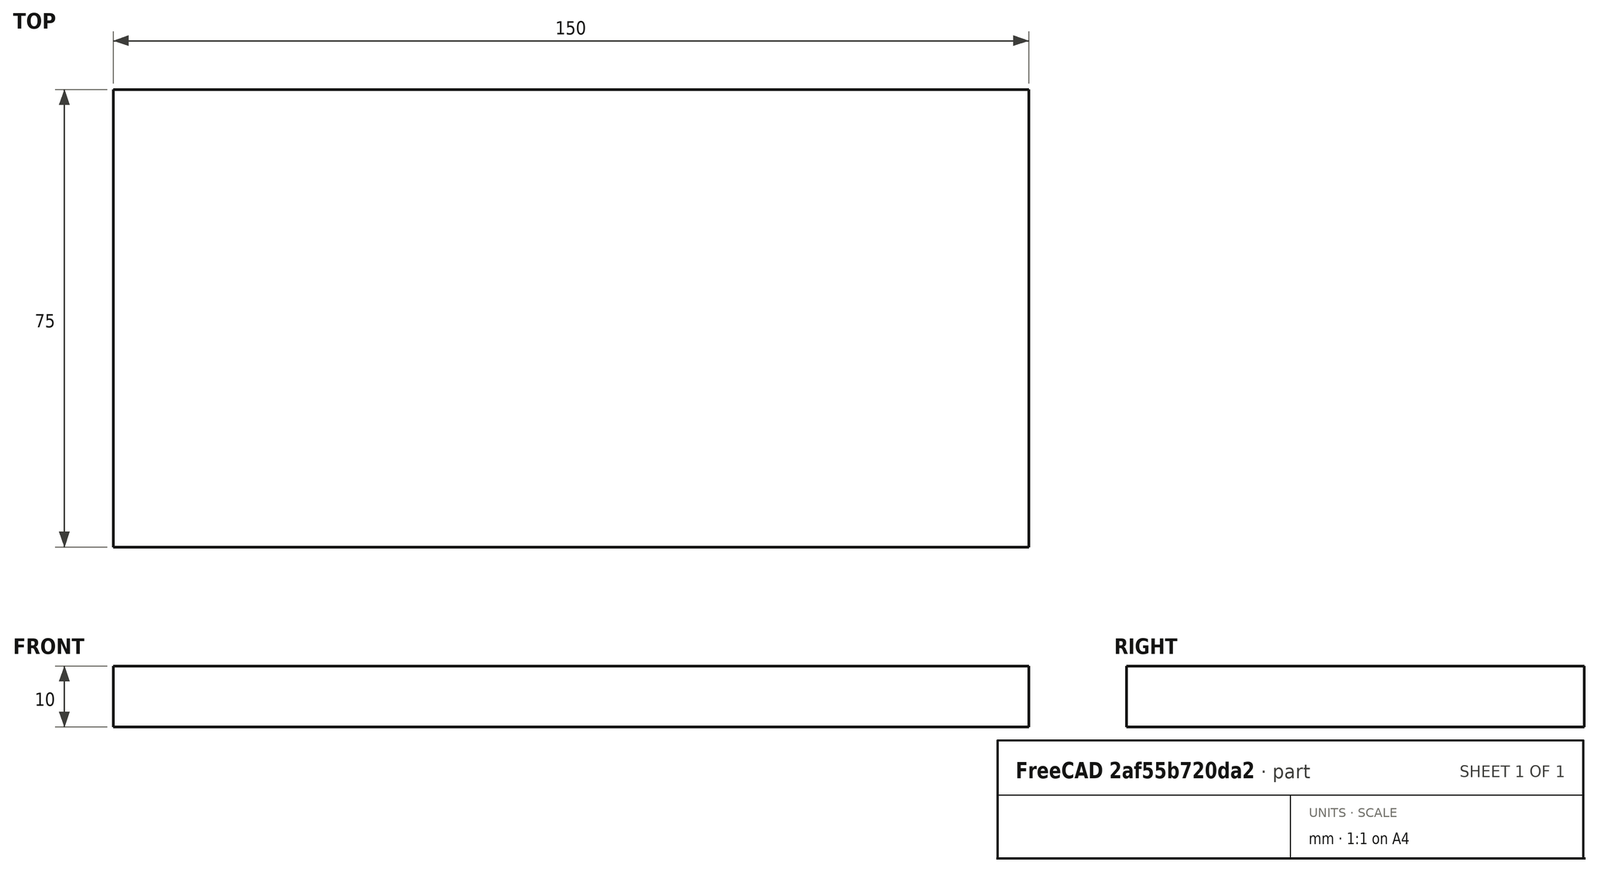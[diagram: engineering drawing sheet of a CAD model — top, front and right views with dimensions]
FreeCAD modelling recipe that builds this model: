
FCSTD DOCUMENT  (FreeCAD 0.20R29410 (Git))
Label: BasePlate
License: All rights reserved
LicenseURL: http://en.wikipedia.org/wiki/All_rights_reserved
objects: Sketcher::SketchObject×1, PartDesign::Pad×1, PartDesign::Body×1
note: 4 computed .brp shape members not serialized (recipe doc carries the construction recipe); baked Part::Feature solids carry a one-line shape summary decoded from their .brp

FEATURE [Sketcher::SketchObject] Sketch
  FullyConstrained = true
  MapMode = 5
  Support = -> [XY_Plane]
  sketch-geometry (5):
    g0: GeomPoint X=0 Y=0 Z=0
    g1: LineSegment StartX=0 StartY=0 StartZ=0 EndX=150 EndY=0 EndZ=0
    g2: LineSegment StartX=150 StartY=0 StartZ=0 EndX=150 EndY=-75 EndZ=0
    g3: LineSegment StartX=150 StartY=-75 StartZ=0 EndX=0 EndY=-75 EndZ=0
    g4: LineSegment StartX=0 StartY=-75 StartZ=0 EndX=0 EndY=0 EndZ=0
  constraints (12):
    c: Coincident(g0,g-1)
    c: Coincident(g1,g2)
    c: Coincident(g2,g3)
    c: Coincident(g3,g4)
    c: Coincident(g4,g1)
    c: Horizontal(g1)
    c: Horizontal(g3)
    c: Vertical(g2)
    c: Vertical(g4)
    c: DistanceX(g1,g1) = 150
    c: DistanceY(g2,g2) = 75
    c: Coincident(g1,g0)
FEATURE [PartDesign::Pad] Pad
  Direction = (0,0,1)
  Length = 10
  Length2 = 10
  Profile = -> Sketch
  ReferenceAxis = -> Sketch [N_Axis]
  Reversed = true
  Type = 0
FEATURE [PartDesign::Body] Body
  Group = -> [Sketch,Pad]
  Origin = -> Origin
  Tip = -> Pad
